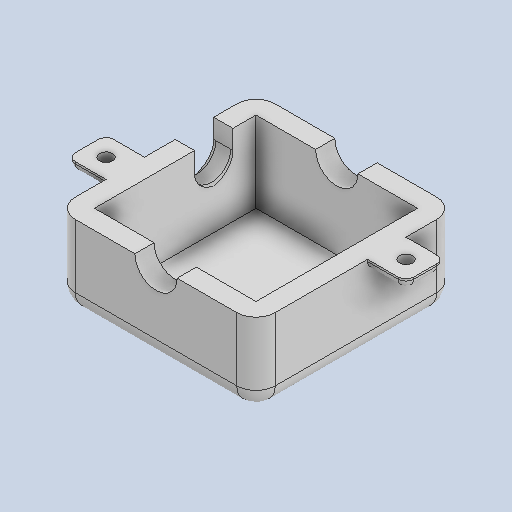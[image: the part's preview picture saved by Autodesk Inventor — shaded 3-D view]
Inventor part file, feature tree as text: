
AUTODESK INVENTOR PART (.ipt)
format: ipt  version: 2023.2 (Build 272271000, 271)  size: 230,400 bytes
history: native  units: in
note: dims shown in document units (in); Inventor stores cm internally (conversion verified against a paired STEP export)
features: sketch x14, other x3
ambient origin geometry x8: Origin, YZ Plane, XZ Plane, XY Plane, X Axis, Y Axis, Z Axis, Center Point
bodies: Solid1 (feature_tree)
feature tree (17):
  other  "kab-f - u.ipt"
  other  "Solid1::kab-f - u.ipt"
  other  "TaggingFeature1"
  sketch  "Sketch1"  dims[d0=0.3937in]
  sketch  "Sketch2"
  sketch  "Sketch3"
  sketch  "Sketch5"
  sketch  "Sketch6"
  sketch  "Sketch11"
  sketch  "Sketch12"
  sketch  "Sketch13"
  sketch  "Sketch14"
  sketch  "Sketch15"
  sketch  "Sketch16"
  sketch  "Sketch17"
  sketch  "Sketch18"
  sketch  "Sketch19"
